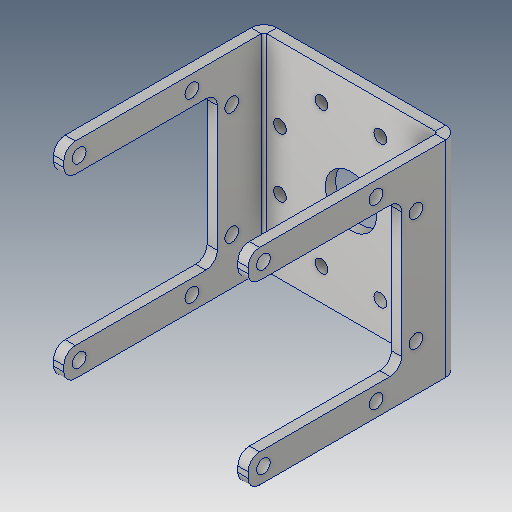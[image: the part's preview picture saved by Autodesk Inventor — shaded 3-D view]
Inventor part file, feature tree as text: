
AUTODESK INVENTOR PART (.ipt)
format: ipt  version: 2020.5 (Build 245400000, 400)  size: 352,768 bytes
history: native  units: mm
features: other x5, extrude x3, sketch x3, fillet x1, projected_geometry x1
ambient origin geometry x8: Origin, YZ Plane, XZ Plane, XY Plane, X Axis, Y Axis, Z Axis, Center Point
bodies: Body1 (feature_tree)
feature tree (13):
  other  "솔리드1"
  extrude  "돌출1"  Depth=34.0mm
  other  "플랜지1"
  extrude  "돌출2"  Depth=17.0mm
  extrude  "돌출8"  Depth=40.2mm
  fillet  "모깎기4"  Radius=20.1mm
  sketch  "스케치1"
  sketch  "스케치2"
  other  "절곡부1"
  other  "구석1"
  sketch  "스케치3"
  projected_geometry  "투영된 루프1"
  other  "정의1"
